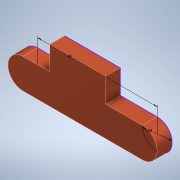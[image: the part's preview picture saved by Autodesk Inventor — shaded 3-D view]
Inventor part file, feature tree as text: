
AUTODESK INVENTOR PART (.ipt)
format: ipt  version: 2022 (Build 260153000, 153)  size: 108,544 bytes
history: native  units: mm
features: extrude x2, sketch x1
ambient origin geometry x8: Origin, YZ Plane, XZ Plane, XY Plane, X Axis, Y Axis, Z Axis, Center Point
bodies: Solid1 (feature_tree)
feature tree (3):
  sketch  "Sketch1"  dims[d0=10.0mm d2=40.0mm d3=5.0mm d4=0.0mm d7=5.0mm d8=0.0mm]
  extrude  "Extrusion1"  Depth=5.0mm
  extrude  "Extrusion3"  Depth=5.0mm TaperAngle=0.0deg
